# Revit family: DC_Rheem_PLM_Raypak_B0972HWT
name_source: partatom
category: Plumbing Fixtures
units: mm (PartAtom-declared; Revit-internal decimal feet)

## family parameters
Cut with Voids When Loaded = No
Host = Face
Part Type = Normal
Room Calculation Point = No
Round Connector Dimension = Use Radius
Shared = No

## types (4) — shared parameters
BoxHeight_ANZRS = 860 mm  [stored 2.82152 ft]
ColdWaterPipeDiameter_ANZRS = 65 mm  [stored 0.213255 ft]
ColdWaterPipeRadius_ANZRS = 33 mm
ConnectorHeight_ANZRS = 755 mm
Description = Raypak - Gas Water Heater- Outdoor - 976 MJ/h  Natural gas, modulating gas control
GasInletHeight_ANZRS = 410 mm
Height_ANZRS = 2500 mm  [stored 8.2021 ft]
HotWaterPipeDiameter_ANZRS = 65 mm  [stored 0.213255 ft]
HotWaterPipeRadius_ANZRS = 33 mm
Length_ANZRS = 1330 mm
Manufacturer = Raypak
Materials_ANZRS = Raypak - Grey Powder Coated Steel
PRVDiameter_ANZRS = 15 mm  [stored 0.0492126 ft]
PRVRadius_ANZRS = 8 mm  [stored 0.0262467 ft]
URL = http://www.rheem.com.au
Width_ANZRS = 825 mm
zero-valued in all types: Default Elevation

## per-type parameters (varying)
| type | GasInletDiameter_ANZRS | GasInletRadius_ANZRS | Model | Type Comments |
| Raypak - Gas Water Heater- Outdoor - 976 MJ/h  Natural gas, modulating gas control | 40 mm  [stored 0.131234 ft] | 20 mm  [stored 0.0656168 ft] | B0976NCM/HWT | Recovery 3784L/h @ 50oC rise |
| Raypak - Gas Water Heater- Outdoor - 976 MJ/h  Natural gas, On/Off gas control | 40 mm  [stored 0.131234 ft] | 20 mm  [stored 0.0656168 ft] | B0976NCO/HWT | Recovery 3784L/h @ 50oC rise |
| Raypak - Gas Water Heater- Outdoor - 933 MJ/h  Propane gas, modulating gas control | 20 mm  [stored 0.0656168 ft] | 10 mm  [stored 0.0328084 ft] | B0976PCM/HWT | Recovery 3526L/h @ 50oC rise |
| Raypak - Gas Water Heater- Outdoor - 933 MJ/h  Propane gas, On/Off gas control | 32 mm  [stored 0.104987 ft] | 16 mm  [stored 0.0524934 ft] | B0976PCO/HWT | Recovery 3526L/h @ 50oC rise |

note: [stored X ft] marks values corroborated as IEEE doubles in the binary element streams (Revit-internal decimal feet)

## geometry (parser evidence)
native form markers: Blend x4, Sweep x2
no freeform markers — native parametric forms only
